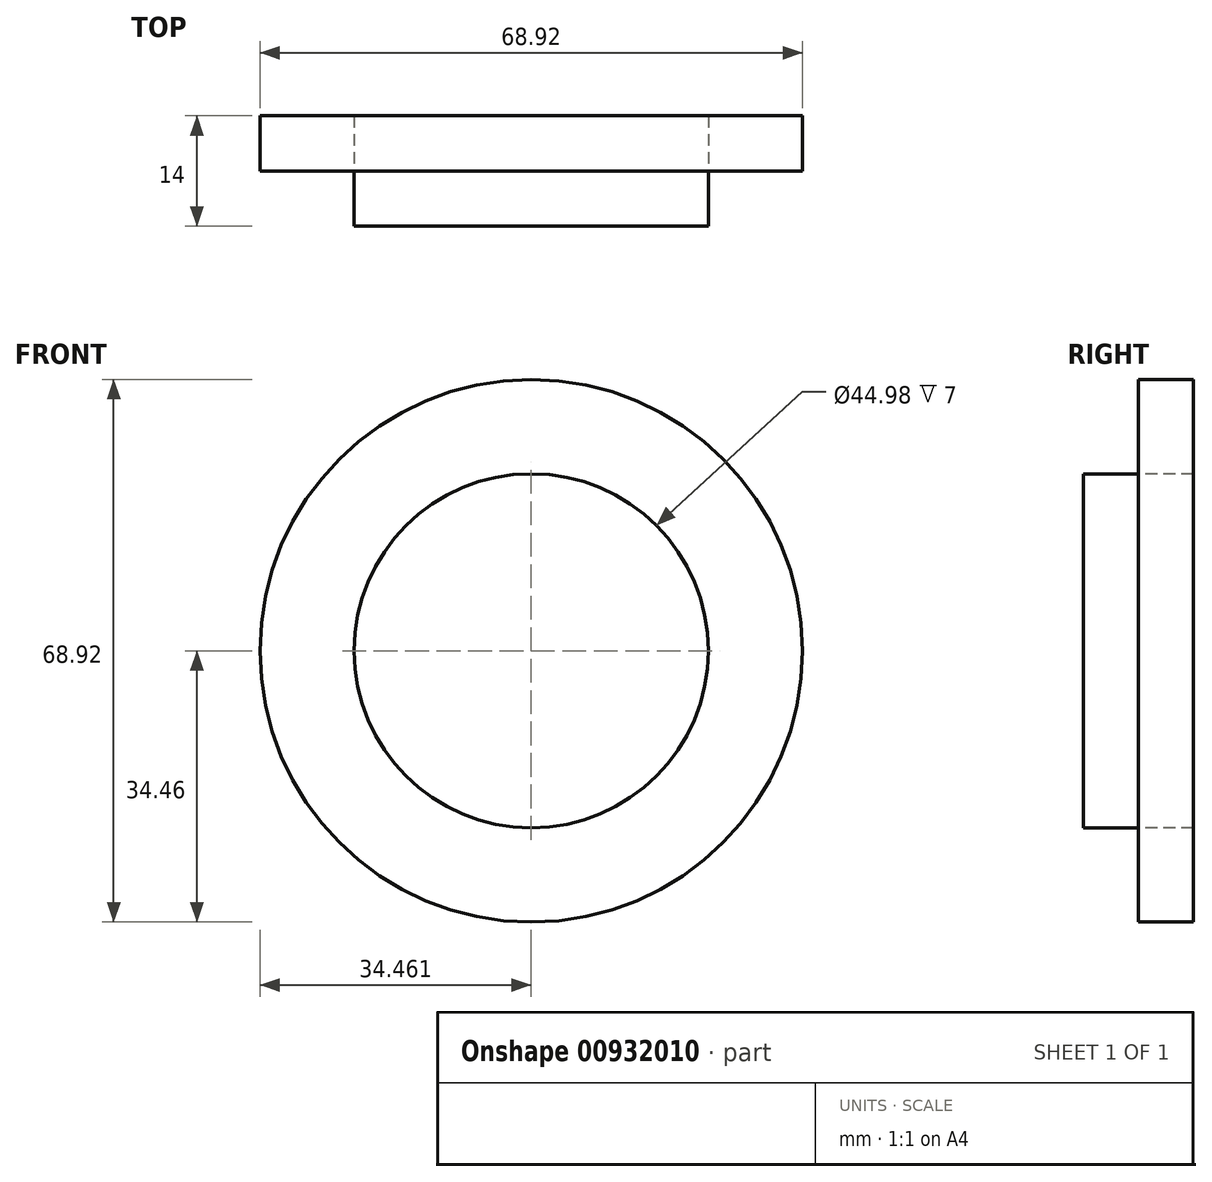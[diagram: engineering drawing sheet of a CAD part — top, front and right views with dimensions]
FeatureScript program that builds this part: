
annotation { "Feature Type Name" : "Feature", "Feature Type Description" : "" }
export const myFeature = defineFeature(function(context is Context, id is Id, definition is map)
    precondition{}
    {
        {
            var Q0;
            Q0=qCreatedBy(makeId("Front.planeOp"),FACE);
            var sketch = newSketch(context, id + "F0", { "sketchPlane" : qUnion([Q0])});
            skCircle(sketch, "E0", {"center": v(-111.47, 33.75) * mm, "radius": 34.46 * mm});
            skCircle(sketch, "E1", {"center": v(-111.47, 33.75) * mm, "radius": 22.5 * mm});
            skSolve(sketch);
        }
        {
            var Q0;
            Q0=makeQuery(id+"F0.imprint","IMPRINT",FACE,{"disambiguationData":[TD([[makeQuery(id+"F0.imprint","IMPRINT",EDGE,{"derivedFrom":sQuery(id+"F0.wireOp",EDGE,"E1")}),1.0]])]});
            extrude(context, id + "F1", {"entities" : qUnion([Q0]), "depth" : 7 * mm, "offsetDistance" : 25 * mm});
        }
        {
            var Q0;
            Q0 = qSketchRegion(id + "F0", true);
            extrude(context, id + "F2", {"entities" : qUnion([Q0]), "oppositeDirection" : true, "depth" : 7 * mm, "offsetDistance" : 25 * mm});
        }
    });
